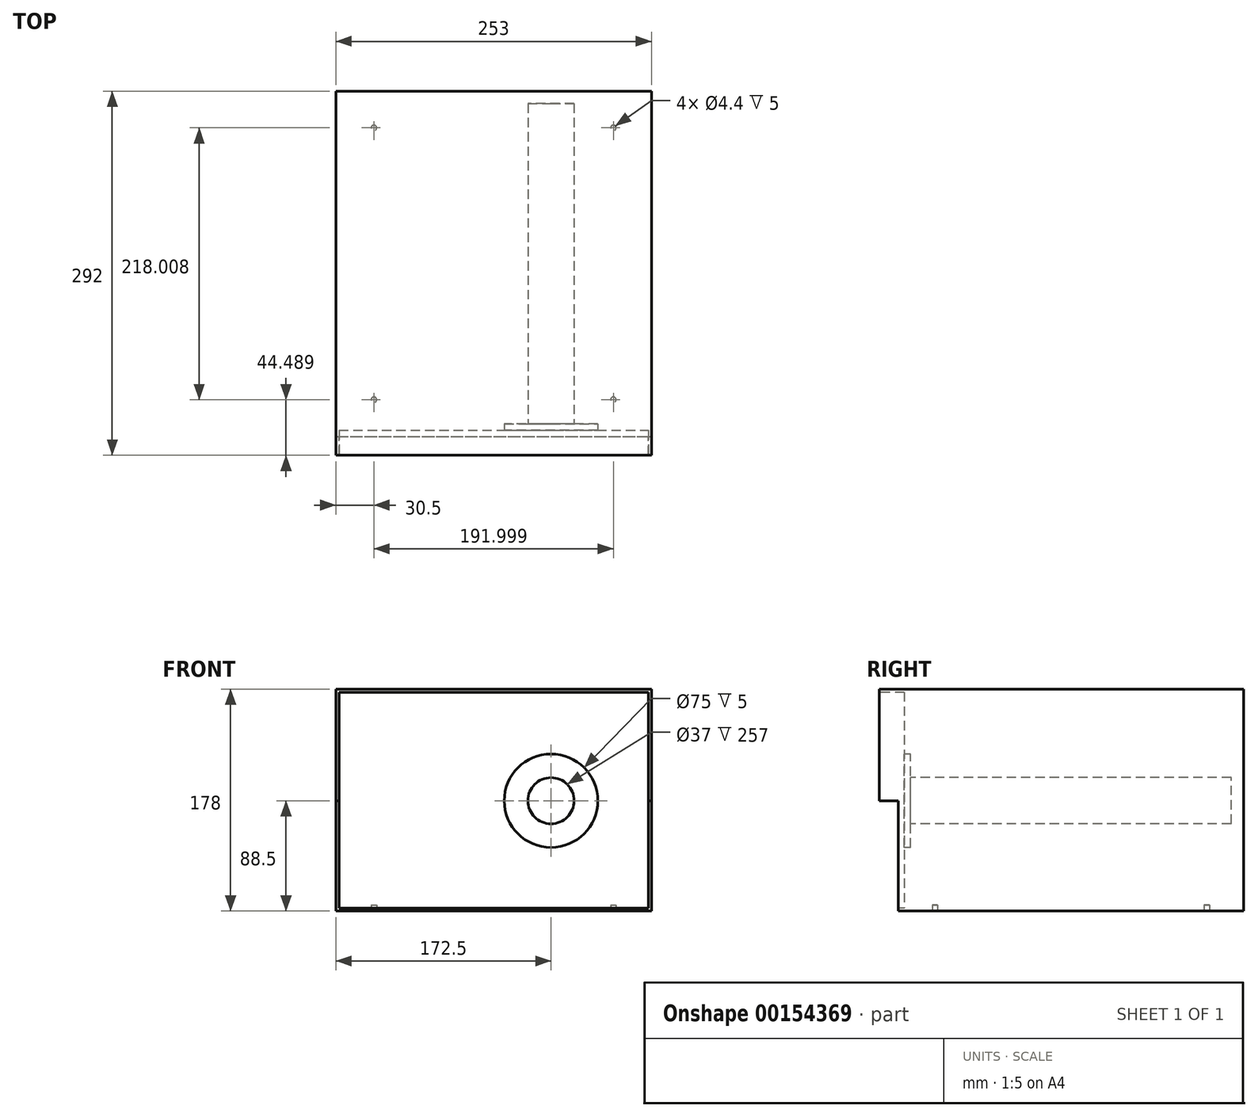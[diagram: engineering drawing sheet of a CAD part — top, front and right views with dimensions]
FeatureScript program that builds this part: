
annotation { "Feature Type Name" : "Feature", "Feature Type Description" : "" }
export const myFeature = defineFeature(function(context is Context, id is Id, definition is map)
    precondition{}
    {
        {
            var Q0;
            Q0=qCreatedBy(makeId("Top.planeOp"),FACE);
            var sketch = newSketch(context, id + "F0", { "sketchPlane" : qUnion([Q0])});
            skLineSegment(sketch, "E0.bottom", {"start": v(-126.5, -138.5) * mm, "end": v(126.5, -138.5) * mm});
            skLineSegment(sketch, "E0.top", {"start": v(-126.5, 138.5) * mm, "end": v(126.5, 138.5) * mm});
            skLineSegment(sketch, "E0.left", {"start": v(-126.5, -138.5) * mm, "end": v(-126.5, 138.5) * mm});
            skLineSegment(sketch, "E0.right", {"start": v(126.5, -138.5) * mm, "end": v(126.5, 138.5) * mm});
            skLineSegment(sketch, "E1", {"start": v(-126.5, -138.5) * mm, "end": v(126.5, 138.5) * mm, "construction": true});
            skSolve(sketch);
        }
        {
            var Q0;
            Q0=makeQuery(id+"F0.imprint","IMPRINT",FACE,{"disambiguationData":[TD([[makeQuery(id+"F0.imprint","IMPRINT",EDGE,{"derivedFrom":sQuery(id+"F0.wireOp",EDGE,"E0.bottom")}),1.0]])]});
            extrude(context, id + "F1", {"entities" : qUnion([Q0]), "depth" : 178 * mm});
        }
        {
            var Q0;
            Q0=makeQuery(id+"F1.opExtrude","SWEPT_FACE",FACE,{"disambiguationData":[OSD([sQuery(id+"F0.wireOp",EDGE,"E0.bottom")])]});
            var sketch = newSketch(context, id + "F2", { "sketchPlane" : qUnion([Q0])});
            skLineSegment(sketch, "E2", {"start": v(46, 178) * mm, "end": v(46, 0) * mm, "construction": true});
            skLineSegment(sketch, "E3", {"start": v(126.5, 88.5) * mm, "end": v(-126.5, 88.5) * mm, "construction": true});
            skCircle(sketch, "E4", {"center": v(46, 88.5) * mm, "radius": 37.5 * mm});
            skLineSegment(sketch, "E5.bottom", {"start": v(-124, 175.5) * mm, "end": v(124, 175.5) * mm});
            skLineSegment(sketch, "E5.top", {"start": v(-124, 2.5) * mm, "end": v(124, 2.5) * mm});
            skLineSegment(sketch, "E5.left", {"start": v(-124, 175.5) * mm, "end": v(-124, 2.5) * mm});
            skLineSegment(sketch, "E5.right", {"start": v(124, 175.5) * mm, "end": v(124, 2.5) * mm});
            skSolve(sketch);
        }
        {
            var Q0;
            Q0=makeQuery(id+"F2.imprint","IMPRINT",FACE,{"disambiguationData":[TD([[makeQuery(id+"F2.imprint","IMPRINT",EDGE,{"derivedFrom":sQuery(id+"F2.wireOp",EDGE,"E4")}),-1.0]])]});
            extrude(context, id + "F3", {"entities" : qUnion([Q0]), "operationType" : NewBodyOperationType.REMOVE, "oppositeDirection" : true, "depth" : 5 * mm});
        }
        {
            var Q0;
            {var subQ1=sQuery(id+"F0.wireOp",EDGE,"E0.left");var subQ3=sQuery(id+"F0.wireOp",EDGE,"E0.bottom");Q0=makeQuery(id+"F3.boolean.opBoolean","SPLIT",FACE,{"disambiguationData":[TD([makeQuery(id+"F1.opExtrude","SWEPT_FACE",FACE,{"disambiguationData":[OSD([subQ1])]})])],"derivedFrom":makeQuery(id+"F1.opExtrude","SWEPT_FACE",FACE,{"disambiguationData":[OSD([subQ3])]})});}
            var sketch = newSketch(context, id + "F4", { "sketchPlane" : qUnion([Q0])});
            skLineSegment(sketch, "E6", {"start": v(-126.5, 88.5) * mm, "end": v(-124, 88.5) * mm});
            skLineSegment(sketch, "E7", {"start": v(124, 88.5) * mm, "end": v(126.5, 88.5) * mm});
            skSolve(sketch);
        }
        {
            var Q0;
            {var subQ4=sQuery(id+"F4.wireOp",EDGE,"E6");Q0=makeQuery(id+"F4.imprint","IMPRINT",FACE,{"disambiguationData":[TD([[makeQuery(id+"F4.imprint","IMPRINT",EDGE,{"derivedFrom":subQ4}),1.0]])]});}
            extrude(context, id + "F5", {"entities" : qUnion([Q0]), "operationType" : NewBodyOperationType.ADD, "depth" : 15 * mm});
        }
        {
            var Q0;
            Q0=makeQuery(id+"F3.boolean.opBoolean","SPLIT",FACE,{"disambiguationData":[TD([makeQuery(id+"F3.opExtrude","SWEPT_FACE",FACE,{"disambiguationData":[OSD([sQuery(id+"F2.wireOp",EDGE,"E4")])]})])],"derivedFrom":makeQuery(id+"F1.opExtrude","SWEPT_FACE",FACE,{"disambiguationData":[OSD([sQuery(id+"F0.wireOp",EDGE,"E0.bottom")])]})});
            extrude(context, id + "F6", {"entities" : qUnion([Q0]), "operationType" : NewBodyOperationType.REMOVE, "oppositeDirection" : true, "depth" : 10 * mm});
        }
        {
            var Q0;
            Q0=makeQuery(id+"F6.boolean.opBoolean","COPY",FACE,{"derivedFrom":makeQuery(id+"F6.opExtrude","CAP_FACE",FACE,{"disambiguationData":[OSD([sQuery(id+"F0.wireOp",EDGE,"E0.bottom")])],"isStart":false})});
            var sketch = newSketch(context, id + "F7", { "sketchPlane" : qUnion([Q0])});
            skCircle(sketch, "E8", {"center": v(46, 88.5) * mm, "radius": 18.5 * mm});
            skSolve(sketch);
        }
        {
            var Q0;
            Q0=makeQuery(id+"F7.imprint","IMPRINT",FACE,{"disambiguationData":[TD([[makeQuery(id+"F7.imprint","IMPRINT",EDGE,{"derivedFrom":sQuery(id+"F7.wireOp",EDGE,"E8")}),1.0]])]});
            extrude(context, id + "F8", {"entities" : qUnion([Q0]), "operationType" : NewBodyOperationType.REMOVE, "oppositeDirection" : true, "depth" : 257 * mm});
        }
        {
            var Q0;
            Q0=makeQuery(id+"F1.opExtrude","CAP_FACE",FACE,{"disambiguationData":[OSD([sQuery(id+"F0.wireOp",EDGE,"E0.bottom"),sQuery(id+"F0.wireOp",EDGE,"E0.top"),sQuery(id+"F0.wireOp",EDGE,"E0.left"),sQuery(id+"F0.wireOp",EDGE,"E0.right")])],"isStart":true});
            var sketch = newSketch(context, id + "F9", { "sketchPlane" : qUnion([Q0])});
            skLineSegment(sketch, "E9", {"start": v(0, 138.5) * mm, "end": v(0, -138.5) * mm, "construction": true});
            skLineSegment(sketch, "E10", {"start": v(-96, 138.5) * mm, "end": v(-96, -138.5) * mm, "construction": true});
            skLineSegment(sketch, "E11", {"start": v(96, 138.5) * mm, "end": v(96, -138.5) * mm, "construction": true});
            skLineSegment(sketch, "E12", {"start": v(-126.5, -109) * mm, "end": v(126.5, -109) * mm, "construction": true});
            skLineSegment(sketch, "E13", {"start": v(-126.5, 109.01) * mm, "end": v(126.5, 109.01) * mm, "construction": true});
            skCircle(sketch, "E14", {"center": v(-96, -109) * mm, "radius": 2.2 * mm});
            skCircle(sketch, "E15", {"center": v(96, -109) * mm, "radius": 2.2 * mm});
            skCircle(sketch, "E16", {"center": v(96, 109.01) * mm, "radius": 2.2 * mm});
            skCircle(sketch, "E17", {"center": v(-96, 109.01) * mm, "radius": 2.2 * mm});
            skSolve(sketch);
        }
        {
            var Q0;
            Q0=makeQuery(id+"F9.imprint","IMPRINT",FACE,{"disambiguationData":[TD([[makeQuery(id+"F9.imprint","IMPRINT",EDGE,{"derivedFrom":sQuery(id+"F9.wireOp",EDGE,"E17")}),1.0]])]});
            var Q1;
            Q1=makeQuery(id+"F9.imprint","IMPRINT",FACE,{"disambiguationData":[TD([[makeQuery(id+"F9.imprint","IMPRINT",EDGE,{"derivedFrom":sQuery(id+"F9.wireOp",EDGE,"E16")}),1.0]])]});
            var Q2;
            Q2=makeQuery(id+"F9.imprint","IMPRINT",FACE,{"disambiguationData":[TD([[makeQuery(id+"F9.imprint","IMPRINT",EDGE,{"derivedFrom":sQuery(id+"F9.wireOp",EDGE,"E14")}),1.0]])]});
            var Q3;
            Q3=makeQuery(id+"F9.imprint","IMPRINT",FACE,{"disambiguationData":[TD([[makeQuery(id+"F9.imprint","IMPRINT",EDGE,{"derivedFrom":sQuery(id+"F9.wireOp",EDGE,"E15")}),1.0]])]});
            extrude(context, id + "F10", {"entities" : qUnion([Q0, Q1, Q2, Q3]), "operationType" : NewBodyOperationType.REMOVE, "oppositeDirection" : true, "depth" : 5 * mm});
        }
    });
